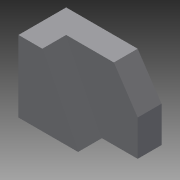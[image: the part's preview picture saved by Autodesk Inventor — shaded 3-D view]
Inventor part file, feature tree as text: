
AUTODESK INVENTOR PART (.ipt)
format: ipt  version: 2015 (Build 190159000, 159)  size: 81,920 bytes
history: native  units: in
note: dims shown in document units (in); Inventor stores cm internally (conversion verified against a paired STEP export)
features: extrude x2, sketch x2
ambient origin geometry x8: Origin, YZ Plane, XZ Plane, XY Plane, X Axis, Y Axis, Z Axis, Center Point
bodies: Solid1 (feature_tree)
feature tree (4):
  extrude  "Extrusion1"  Depth=2.0in
  extrude  "Extrusion2"  Depth=0.5in
  sketch  "Sketch1"  dims[d0=1.5in d1=2.0in]
  sketch  "Sketch2"  dims[d2=1.5in d3=0.75in d4=0.5in d5=0.0in d6=0.5in d7=1.25in d8=0.5in d9=0.0in]
